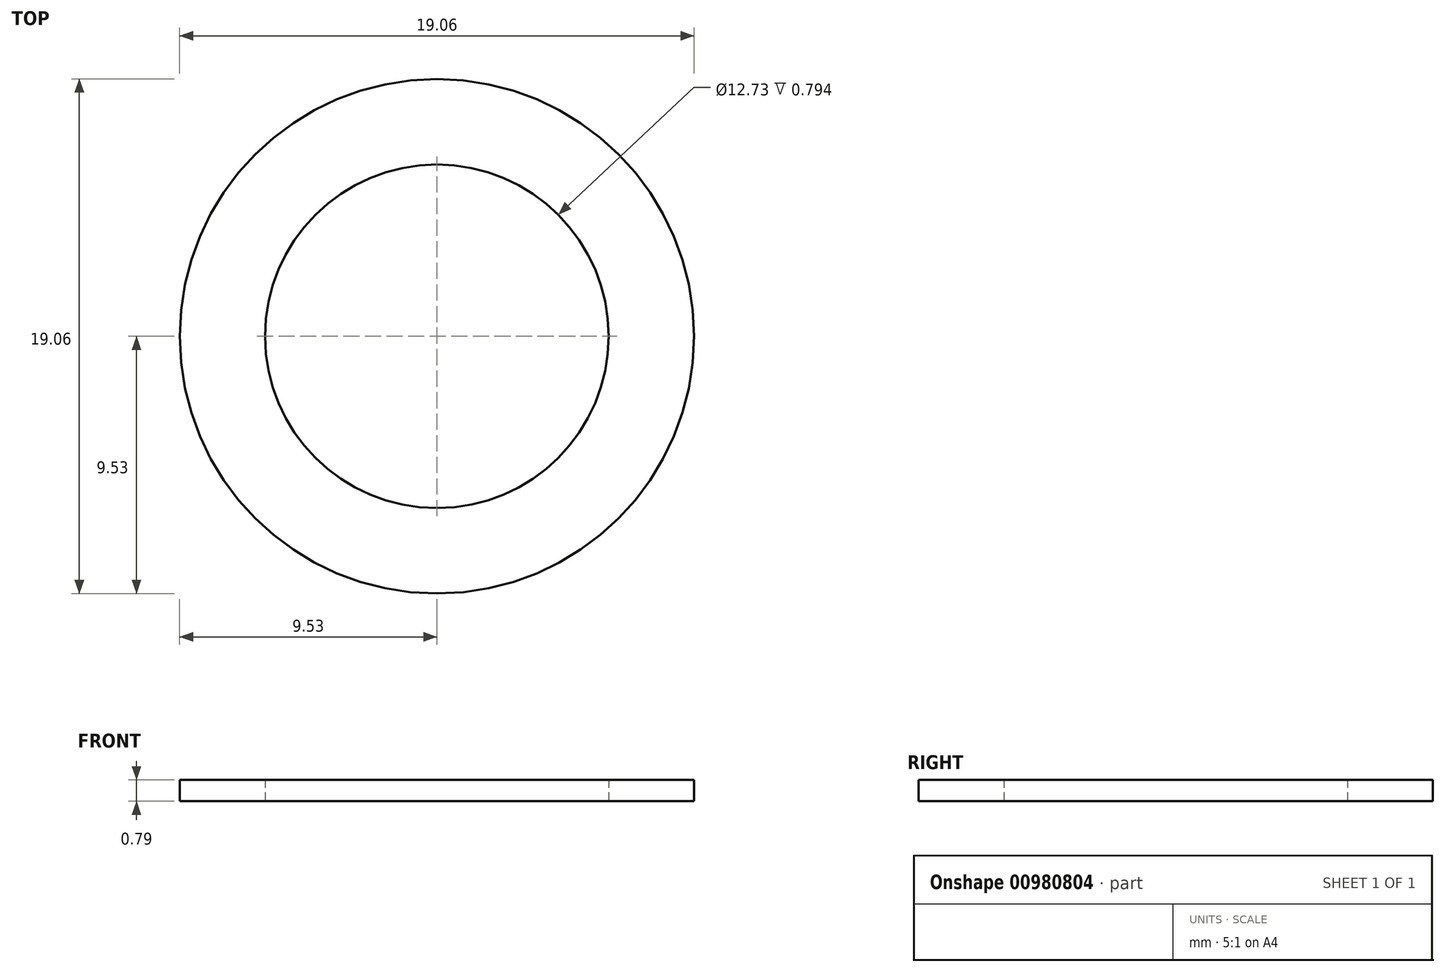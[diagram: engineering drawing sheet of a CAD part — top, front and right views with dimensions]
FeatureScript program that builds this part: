
annotation { "Feature Type Name" : "Feature", "Feature Type Description" : "" }
export const myFeature = defineFeature(function(context is Context, id is Id, definition is map)
    precondition{}
    {
        {
            var Q0;
            Q0=qCreatedBy(makeId("Top.planeOp"),FACE);
            var sketch = newSketch(context, id + "F0", { "sketchPlane" : qUnion([Q0])});
            skCircle(sketch, "E0", {"center": v(0, 0) * mm, "radius": 6.36 * mm});
            skCircle(sketch, "E1", {"center": v(0, 0) * mm, "radius": 9.53 * mm});
            skSolve(sketch);
        }
        {
            var Q0;
            Q0=qSketchRegion(id+"F0",true);
            extrude(context, id + "F1", {"entities" : qUnion([Q0]), "depth" : 0.8 * mm, "offsetDistance" : 25.4 * mm});
        }
    });
